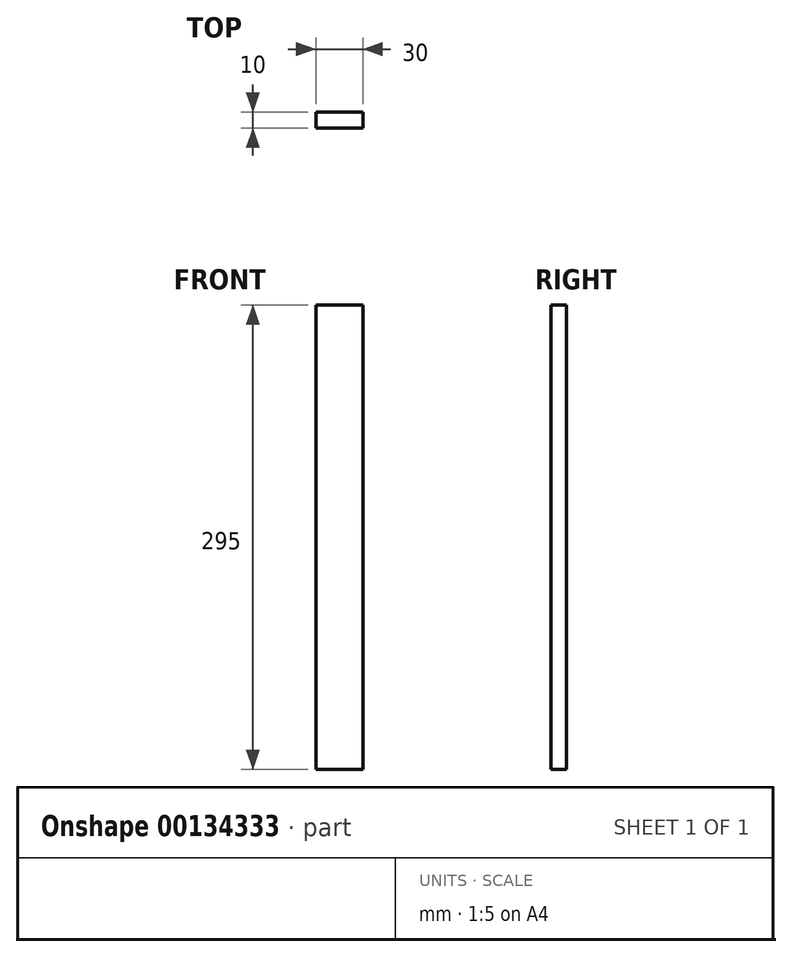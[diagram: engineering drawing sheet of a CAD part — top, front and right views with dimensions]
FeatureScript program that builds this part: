
annotation { "Feature Type Name" : "Feature", "Feature Type Description" : "" }
export const myFeature = defineFeature(function(context is Context, id is Id, definition is map)
    precondition{}
    {
        {
            var Q0;
            Q0=qCreatedBy(makeId("Front.planeOp"),FACE);
            var sketch = newSketch(context, id + "F0", { "sketchPlane" : qUnion([Q0])});
            skLineSegment(sketch, "E0.bottom", {"start": v(-25.43, 227.25) * mm, "end": v(4.57, 227.25) * mm});
            skLineSegment(sketch, "E0.top", {"start": v(-25.43, -67.75) * mm, "end": v(4.57, -67.75) * mm});
            skLineSegment(sketch, "E0.left", {"start": v(-25.43, 227.25) * mm, "end": v(-25.43, -67.75) * mm});
            skLineSegment(sketch, "E0.right", {"start": v(4.57, 227.25) * mm, "end": v(4.57, -67.75) * mm});
            skSolve(sketch);
        }
        {
            var Q0;
            Q0 = qSketchRegion(id + "F0", true);
            extrude(context, id + "F1", {"entities" : qUnion([Q0]), "depth" : 10 * mm});
        }
    });
